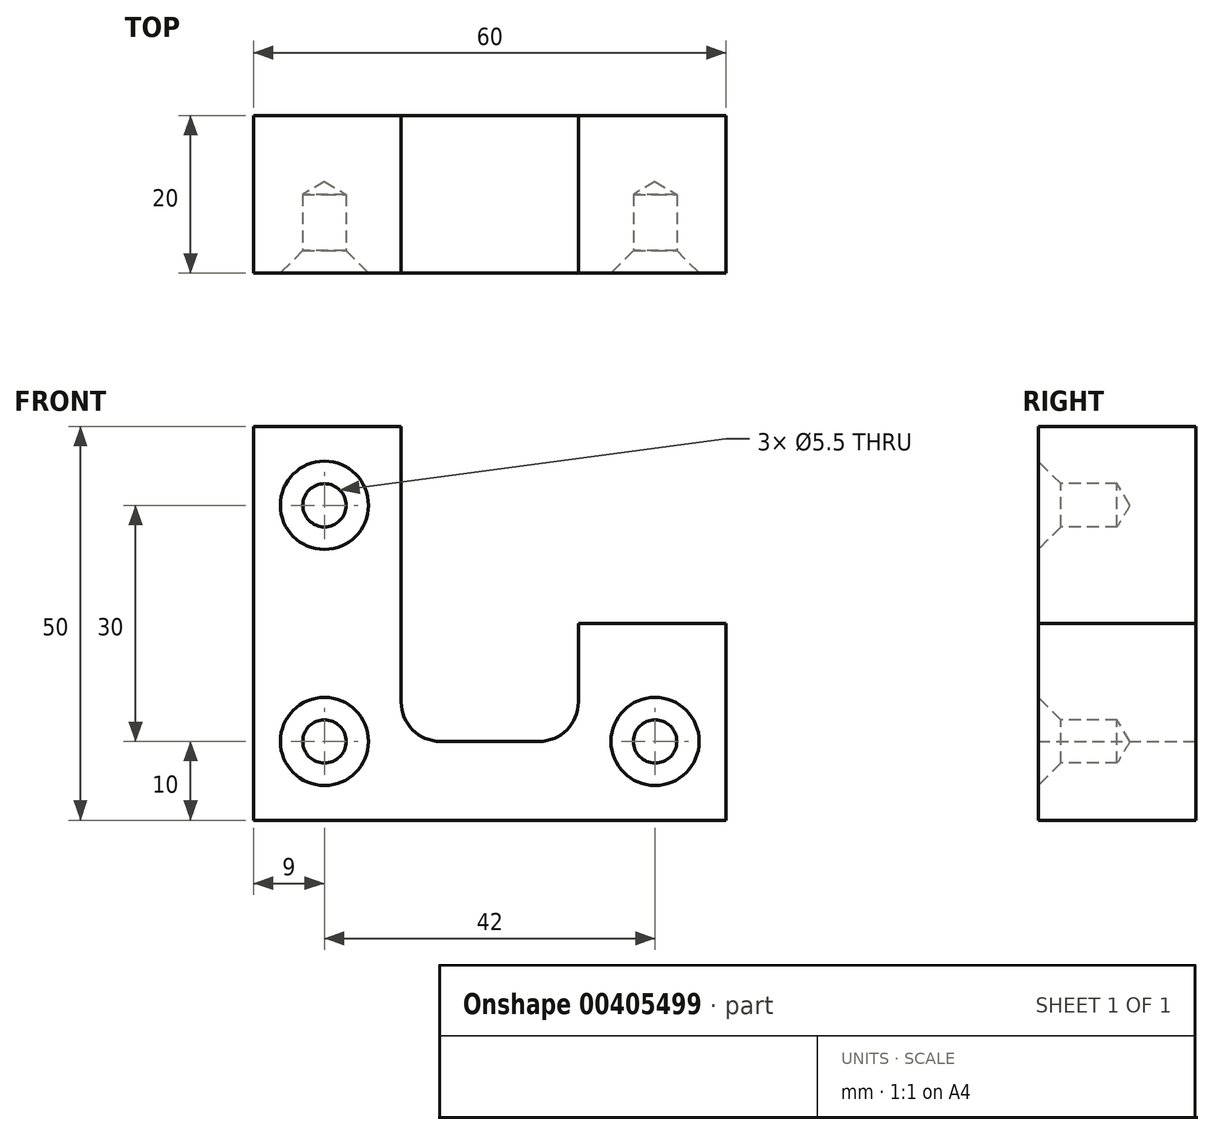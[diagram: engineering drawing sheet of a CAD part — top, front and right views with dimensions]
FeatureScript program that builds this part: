
annotation { "Feature Type Name" : "Feature", "Feature Type Description" : "" }
export const myFeature = defineFeature(function(context is Context, id is Id, definition is map)
    precondition{}
    {
        {
            var Q0;
            Q0=qCreatedBy(makeId("Front.planeOp"),FACE);
            var sketch = newSketch(context, id + "F0", { "sketchPlane" : qUnion([Q0])});
            skLineSegment(sketch, "E0.bottom", {"start": v(0, 0) * mm, "end": v(60, 0) * mm});
            skLineSegment(sketch, "E0.top", {"start": v(0, 50) * mm, "end": v(18.75, 50) * mm});
            skLineSegment(sketch, "E0.left", {"start": v(0, 0) * mm, "end": v(0, 50) * mm});
            skLineSegment(sketch, "E0.right", {"start": v(60, 0) * mm, "end": v(60, 25) * mm});
            skLineSegment(sketch, "E1", {"start": v(18.75, 50) * mm, "end": v(18.75, 10) * mm});
            skLineSegment(sketch, "E2", {"start": v(18.75, 10) * mm, "end": v(41.25, 10) * mm});
            skLineSegment(sketch, "E3", {"start": v(41.25, 10) * mm, "end": v(41.25, 25) * mm});
            skLineSegment(sketch, "E4", {"start": v(41.25, 25) * mm, "end": v(60, 25) * mm});
            skSolve(sketch);
        }
        {
            var Q0;
            Q0=makeQuery(id+"F0.imprint","IMPRINT",FACE,{"disambiguationData":[TD([[makeQuery(id+"F0.imprint","IMPRINT",EDGE,{"derivedFrom":sQuery(id+"F0.wireOp",EDGE,"E0.bottom")}),1.0]])]});
            extrude(context, id + "F1", {"entities" : qUnion([Q0]), "endBound" : BoundingType.SYMMETRIC, "depth" : 20 * mm});
        }
        {
            var Q0;
            Q0=makeQuery(id+"F1.opExtrude","CAP_FACE",FACE,{"disambiguationData":[OSD([sQuery(id+"F0.wireOp",EDGE,"E0.bottom"),sQuery(id+"F0.wireOp",EDGE,"E0.top"),sQuery(id+"F0.wireOp",EDGE,"E0.left"),sQuery(id+"F0.wireOp",EDGE,"E0.right"),sQuery(id+"F0.wireOp",EDGE,"E1"),sQuery(id+"F0.wireOp",EDGE,"E2"),sQuery(id+"F0.wireOp",EDGE,"E3"),sQuery(id+"F0.wireOp",EDGE,"E4")])],"isStart":false});
            var sketch = newSketch(context, id + "F2", { "sketchPlane" : qUnion([Q0])});
            skPoint(sketch, "E5", {"position": v(9, 40) * mm});
            skPoint(sketch, "E6", {"position": v(9, 10) * mm});
            skPoint(sketch, "E7", {"position": v(51, 10) * mm});
            skSolve(sketch);
        }
        {
            var Q0;
            Q0=sQuery(id+"F2.wireOp",VERTEX,"E5");
            var Q1;
            Q1=sQuery(id+"F2.wireOp",VERTEX,"E6");
            var Q2;
            Q2=sQuery(id+"F2.wireOp",VERTEX,"E7");
            var Q3;
            Q3=makeQuery(id+"F1.opExtrude","SWEPT_BODY",BODY,{"disambiguationData":[OSD([sQuery(id+"F0.wireOp",EDGE,"E0.bottom"),sQuery(id+"F0.wireOp",EDGE,"E0.top"),sQuery(id+"F0.wireOp",EDGE,"E0.left"),sQuery(id+"F0.wireOp",EDGE,"E0.right"),sQuery(id+"F0.wireOp",EDGE,"E1"),sQuery(id+"F0.wireOp",EDGE,"E2"),sQuery(id+"F0.wireOp",EDGE,"E3"),sQuery(id+"F0.wireOp",EDGE,"E4")])]});
            hole(context, id + "F3", {"style" : HoleStyle.C_SINK, "endStyle" : HoleEndStyle.BLIND, "standardTappedOrClearance" : lookupTablePath({ "standard" : "ISO", "fit" : "Normal", "size" : "M5", "type" : "Clearance" }), "standardBlindInLast" : lookupTablePath({ "fit" : "Standard", "standard" : "ISO", "size" : "M5", "type" : "Clearance" }), "holeDiameter" : 5.5 * mm, "cSinkDiameter" : 11.2 * mm, "cSinkAngle" : 90 * degree, "holeDepth" : 10 * mm, "isTappedThrough" : true, "tappedDepth" : 7.6 * mm, "tapClearance" : 3, "locations" : qUnion([Q0, Q1, Q2]), "scope" : qUnion([Q3])});
        }
        {
            var Q0;
            Q0=makeQuery(id+"F1.opExtrude","SWEPT_EDGE",EDGE,{"disambiguationData":[OSD([sQuery(id+"F0.wireOp",EDGE,"E2"),sQuery(id+"F0.wireOp",EDGE,"E3")])]});
            var Q1;
            Q1=makeQuery(id+"F1.opExtrude","SWEPT_EDGE",EDGE,{"disambiguationData":[OSD([sQuery(id+"F0.wireOp",EDGE,"E1"),sQuery(id+"F0.wireOp",EDGE,"E2")])]});
            fillet(context, id + "F4", {"entities" : qUnion([Q0, Q1]), "radius" : 5 * mm, "tangentPropagation" : true, "allowEdgeOverflow" : false});
        }
    });
